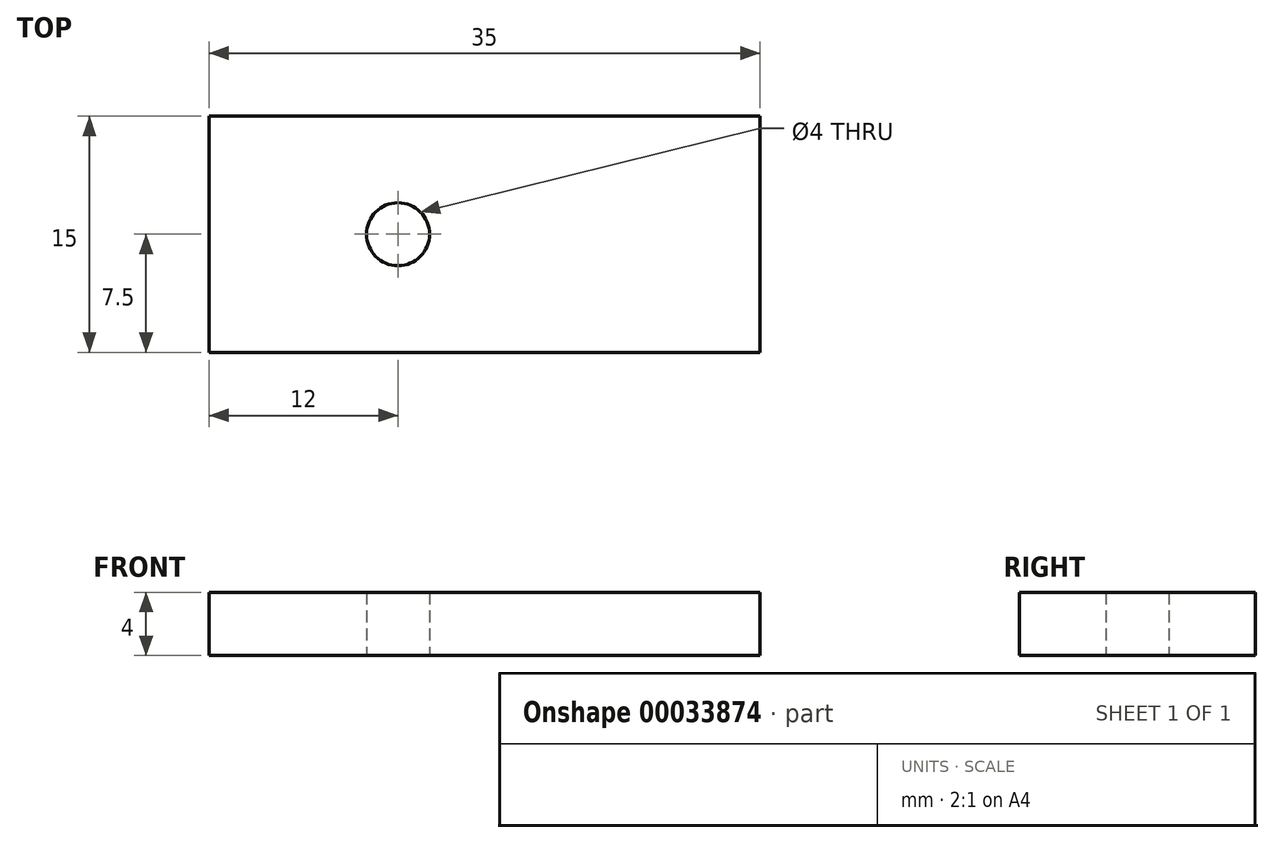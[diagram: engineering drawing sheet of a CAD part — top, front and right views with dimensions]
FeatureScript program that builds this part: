
annotation { "Feature Type Name" : "Feature", "Feature Type Description" : "" }
export const myFeature = defineFeature(function(context is Context, id is Id, definition is map)
    precondition{}
    {
        {
            var Q0;
            Q0=qCreatedBy(makeId("Top.planeOp"),FACE);
            var sketch = newSketch(context, id + "F0", { "sketchPlane" : qUnion([Q0])});
            skLineSegment(sketch, "E0.bottom", {"start": v(0, 0) * mm, "end": v(35, 0) * mm});
            skLineSegment(sketch, "E0.top", {"start": v(0, -15) * mm, "end": v(35, -15) * mm});
            skLineSegment(sketch, "E0.left", {"start": v(0, 0) * mm, "end": v(0, -15) * mm});
            skLineSegment(sketch, "E0.right", {"start": v(35, 0) * mm, "end": v(35, -15) * mm});
            skCircle(sketch, "E1", {"center": v(12, -7.5) * mm, "radius": 2 * mm});
            skPoint(sketch, "E1.centerSnap0", {"position": v(0, -7.5) * mm});
            skSolve(sketch);
        }
        {
            var Q0;
            Q0 = qSketchRegion(id + "F0", true);
            extrude(context, id + "F1", {"entities" : qUnion([Q0]), "depth" : 4 * mm});
        }
    });
